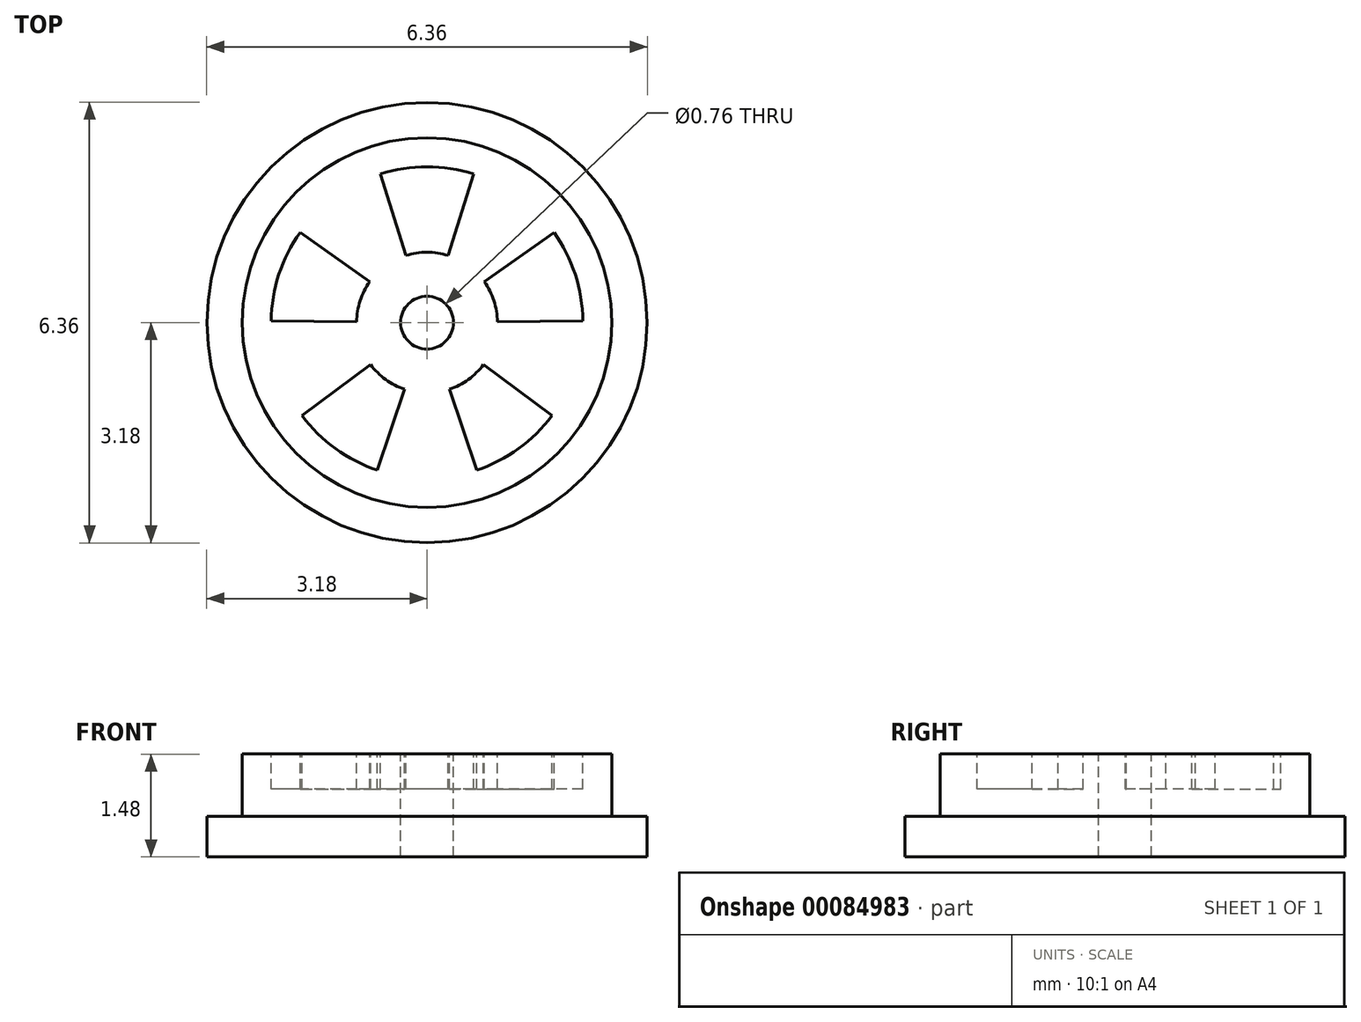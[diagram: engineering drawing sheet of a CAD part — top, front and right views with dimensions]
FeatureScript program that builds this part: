
annotation { "Feature Type Name" : "Feature", "Feature Type Description" : "" }
export const myFeature = defineFeature(function(context is Context, id is Id, definition is map)
    precondition{}
    {
        {
            var Q0;
            Q0=qCreatedBy(makeId("Top.planeOp"),FACE);
            var sketch = newSketch(context, id + "F0", { "sketchPlane" : qUnion([Q0])});
            skCircle(sketch, "E0", {"center": v(0, 0) * mm, "radius": 3.18 * mm});
            skSolve(sketch);
        }
        {
            var Q0;
            Q0 = qSketchRegion(id + "F0", true);
            extrude(context, id + "F1", {"entities" : qUnion([Q0]), "depth" : 0.58 * mm});
        }
        {
            var Q0;
            Q0=makeQuery(id+"F1.opExtrude","CAP_FACE",FACE,{"disambiguationData":[OSD([sQuery(id+"F0.wireOp",EDGE,"E0")])],"isStart":false});
            var sketch = newSketch(context, id + "F2", { "sketchPlane" : qUnion([Q0])});
            skCircle(sketch, "E1", {"center": v(0, 0) * mm, "radius": 2.67 * mm});
            skSolve(sketch);
        }
        {
            var Q0;
            Q0 = qSketchRegion(id + "F2", true);
            extrude(context, id + "F3", {"entities" : qUnion([Q0]), "operationType" : NewBodyOperationType.ADD, "depth" : 0.9 * mm});
        }
        {
            var Q0;
            Q0=makeQuery(id+"F3.opExtrude","CAP_FACE",FACE,{"disambiguationData":[OSD([sQuery(id+"F2.wireOp",EDGE,"E1")])],"isStart":false});
            var sketch = newSketch(context, id + "F4", { "sketchPlane" : qUnion([Q0])});
            skCircle(sketch, "E2", {"center": v(0, 0) * mm, "radius": 0.38 * mm});
            skSolve(sketch);
        }
        {
            var Q0;
            Q0 = qSketchRegion(id + "F4", true);
            extrude(context, id + "F5", {"entities" : qUnion([Q0]), "operationType" : NewBodyOperationType.REMOVE, "oppositeDirection" : true, "depth" : 25.4 * mm});
        }
        {
            var Q0;
            Q0=makeQuery(id+"F3.opExtrude","CAP_FACE",FACE,{"disambiguationData":[OSD([sQuery(id+"F2.wireOp",EDGE,"E1")])],"isStart":false});
            var sketch = newSketch(context, id + "F6", { "sketchPlane" : qUnion([Q0])});
            skArc(sketch, "E3", {"start": v(0.3, 0.97) * mm, "mid": v(0, 1.02) * mm, "end": v(-0.3, 0.97) * mm});
            skArc(sketch, "E4", {"start": v(0.67, 2.15) * mm, "mid": v(0, 2.25) * mm, "end": v(-0.67, 2.15) * mm});
            skLineSegment(sketch, "E5", {"start": v(-0.3, 0.97) * mm, "end": v(-0.67, 2.15) * mm});
            skLineSegment(sketch, "E6", {"start": v(0.67, 2.15) * mm, "end": v(0.3, 0.97) * mm});
            skLineSegment(sketch, "E7.1.0", {"start": v(-1.83, 1.3) * mm, "end": v(-0.83, 0.59) * mm});
            skLineSegment(sketch, "E7.1.1", {"start": v(-1.02, 0.01) * mm, "end": v(-2.25, 0.02) * mm});
            skLineSegment(sketch, "E7.2.0", {"start": v(-1.8, -1.34) * mm, "end": v(-0.82, -0.6) * mm});
            skLineSegment(sketch, "E7.2.1", {"start": v(-0.32, -0.96) * mm, "end": v(-0.72, -2.13) * mm});
            skLineSegment(sketch, "E7.3.0", {"start": v(0.72, -2.13) * mm, "end": v(0.32, -0.96) * mm});
            skLineSegment(sketch, "E7.3.1", {"start": v(0.82, -0.6) * mm, "end": v(1.8, -1.34) * mm});
            skLineSegment(sketch, "E7.4.0", {"start": v(2.25, 0.02) * mm, "end": v(1.02, 0.01) * mm});
            skLineSegment(sketch, "E7.4.1", {"start": v(0.83, 0.59) * mm, "end": v(1.83, 1.3) * mm});
            skArc(sketch, "E8.trimOffspring", {"start": v(1.02, 0.01) * mm, "mid": v(0.97, 0.31) * mm, "end": v(0.83, 0.59) * mm});
            skArc(sketch, "E9.trimOffspring", {"start": v(2.25, 0.02) * mm, "mid": v(2.14, 0.7) * mm, "end": v(1.83, 1.3) * mm});
            skArc(sketch, "E10.trimOffspring", {"start": v(0.72, -2.13) * mm, "mid": v(1.32, -1.82) * mm, "end": v(1.8, -1.34) * mm});
            skArc(sketch, "E11.trimOffspring", {"start": v(0.32, -0.96) * mm, "mid": v(0.6, -0.82) * mm, "end": v(0.82, -0.6) * mm});
            skArc(sketch, "E12.trimOffspring", {"start": v(-0.82, -0.6) * mm, "mid": v(-0.6, -0.82) * mm, "end": v(-0.32, -0.96) * mm});
            skArc(sketch, "E13.trimOffspring", {"start": v(-1.8, -1.34) * mm, "mid": v(-1.32, -1.82) * mm, "end": v(-0.72, -2.13) * mm});
            skArc(sketch, "E14.trimOffspring", {"start": v(-0.83, 0.59) * mm, "mid": v(-0.97, 0.31) * mm, "end": v(-1.02, 0.01) * mm});
            skArc(sketch, "E15.trimOffspring", {"start": v(-1.83, 1.3) * mm, "mid": v(-2.14, 0.7) * mm, "end": v(-2.25, 0.02) * mm});
            skSolve(sketch);
        }
        {
            var Q0;
            Q0 = qSketchRegion(id + "F6", true);
            extrude(context, id + "F7", {"entities" : qUnion([Q0]), "operationType" : NewBodyOperationType.REMOVE, "oppositeDirection" : true, "depth" : 0.5 * mm});
        }
    });
